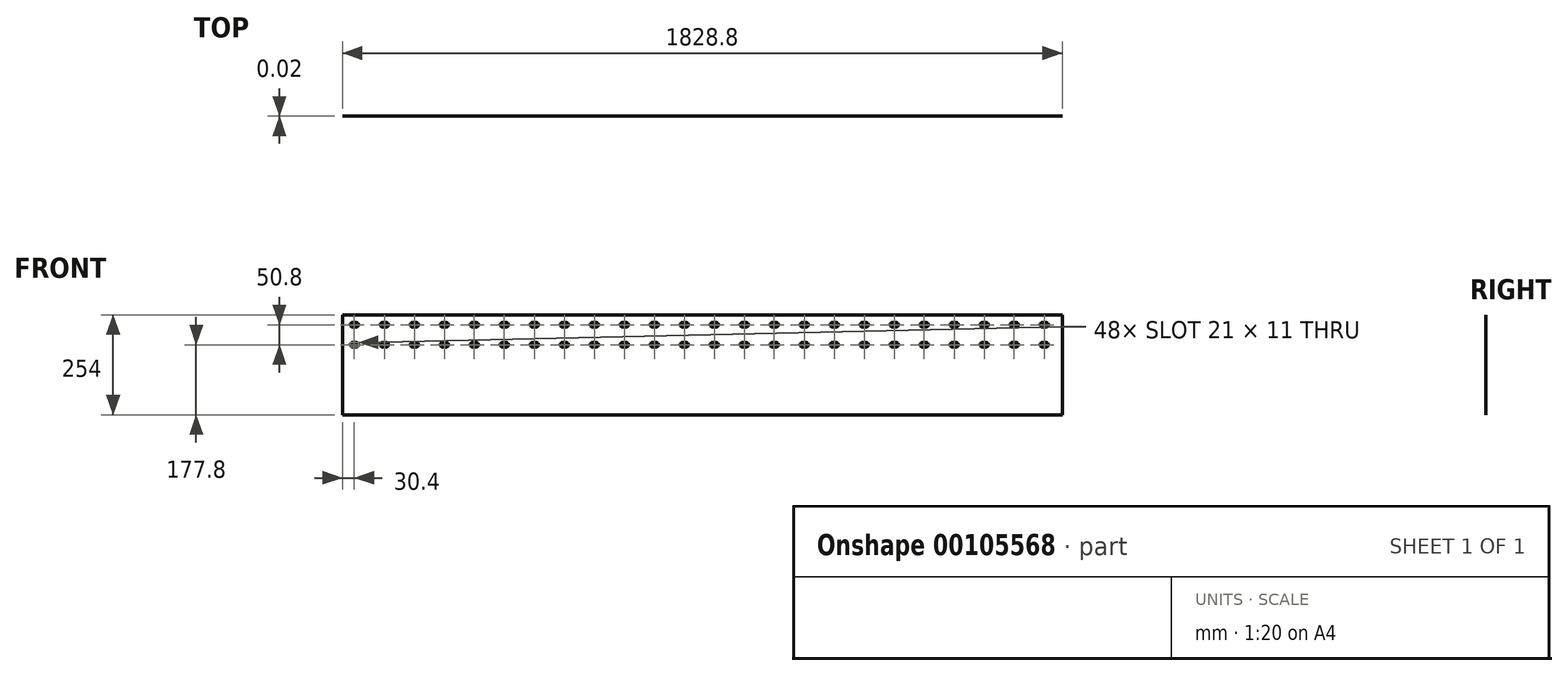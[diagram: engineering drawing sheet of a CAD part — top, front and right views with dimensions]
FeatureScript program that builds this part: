
annotation { "Feature Type Name" : "Feature", "Feature Type Description" : "" }
export const myFeature = defineFeature(function(context is Context, id is Id, definition is map)
    precondition{}
    {
        {
            var Q0;
            Q0=qCreatedBy(makeId("Front.planeOp"),FACE);
            var sketch = newSketch(context, id + "F0", { "sketchPlane" : qUnion([Q0])});
            skLineSegment(sketch, "E0.bottom", {"start": v(1828.8, 254) * mm, "end": v(0, 254) * mm});
            skLineSegment(sketch, "E0.top", {"start": v(1828.8, 0) * mm, "end": v(0, 0) * mm});
            skLineSegment(sketch, "E0.left", {"start": v(1828.8, 254) * mm, "end": v(1828.8, 0) * mm});
            skLineSegment(sketch, "E0.right", {"start": v(0, 254) * mm, "end": v(0, 0) * mm});
            skLineSegment(sketch, "E1", {"start": v(0, 152.4) * mm, "end": v(1828.8, 152.4) * mm, "construction": true});
            skSolve(sketch);
        }
        {
            var Q0;
            Q0=makeQuery(id+"F0.imprint","IMPRINT",FACE,{"disambiguationData":[TD([[makeQuery(id+"F0.imprint","IMPRINT",EDGE,{"derivedFrom":sQuery(id+"F0.wireOp",EDGE,"E0.bottom")}),1.0]])]});
            extrude(context, id + "F1", {"entities" : qUnion([Q0]), "depth" : 0.31 / 50.8 * mm, "hasSecondDirection" : true, "secondDirectionOppositeDirection" : true, "secondDirectionDepth" : 0.31 / 50.8 * mm});
        }
        {
            var Q0;
            Q0=makeQuery(id+"F1.opExtrude","CAP_FACE",FACE,{"disambiguationData":[OSD([sQuery(id+"F0.wireOp",EDGE,"E0.bottom"),sQuery(id+"F0.wireOp",EDGE,"E0.top"),sQuery(id+"F0.wireOp",EDGE,"E0.left"),sQuery(id+"F0.wireOp",EDGE,"E0.right")])],"isStart":false});
            var sketch = newSketch(context, id + "F2", { "sketchPlane" : qUnion([Q0])});
            skArc(sketch, "E2", {"start": v(25.4, 234.1) * mm, "mid": v(19.9, 228.6) * mm, "end": v(25.4, 223.1) * mm});
            skArc(sketch, "E3", {"start": v(35.4, 223.1) * mm, "mid": v(40.9, 228.6) * mm, "end": v(35.4, 234.1) * mm});
            skLineSegment(sketch, "E4", {"start": v(25.4, 234.1) * mm, "end": v(35.4, 234.1) * mm});
            skLineSegment(sketch, "E5", {"start": v(35.4, 223.1) * mm, "end": v(25.4, 223.1) * mm});
            skLineSegment(sketch, "E6.0.1.0", {"start": v(35.4, 172.3) * mm, "end": v(25.4, 172.3) * mm});
            skArc(sketch, "E6.0.1.1", {"start": v(25.4, 183.3) * mm, "mid": v(19.9, 177.8) * mm, "end": v(25.4, 172.3) * mm});
            skLineSegment(sketch, "E6.0.1.2", {"start": v(25.4, 183.3) * mm, "end": v(35.4, 183.3) * mm});
            skArc(sketch, "E6.0.1.3", {"start": v(35.4, 172.3) * mm, "mid": v(40.9, 177.8) * mm, "end": v(35.4, 183.3) * mm});
            skLineSegment(sketch, "E6.1.0.0", {"start": v(111.6, 223.1) * mm, "end": v(101.6, 223.1) * mm});
            skArc(sketch, "E6.1.0.1", {"start": v(101.6, 234.1) * mm, "mid": v(96.1, 228.6) * mm, "end": v(101.6, 223.1) * mm});
            skLineSegment(sketch, "E6.1.0.2", {"start": v(101.6, 234.1) * mm, "end": v(111.6, 234.1) * mm});
            skArc(sketch, "E6.1.0.3", {"start": v(111.6, 223.1) * mm, "mid": v(117.1, 228.6) * mm, "end": v(111.6, 234.1) * mm});
            skLineSegment(sketch, "E6.1.1.0", {"start": v(111.6, 172.3) * mm, "end": v(101.6, 172.3) * mm});
            skArc(sketch, "E6.1.1.1", {"start": v(101.6, 183.3) * mm, "mid": v(96.1, 177.8) * mm, "end": v(101.6, 172.3) * mm});
            skLineSegment(sketch, "E6.1.1.2", {"start": v(101.6, 183.3) * mm, "end": v(111.6, 183.3) * mm});
            skArc(sketch, "E6.1.1.3", {"start": v(111.6, 172.3) * mm, "mid": v(117.1, 177.8) * mm, "end": v(111.6, 183.3) * mm});
            skLineSegment(sketch, "E6.2.0.0", {"start": v(187.8, 223.1) * mm, "end": v(177.8, 223.1) * mm});
            skArc(sketch, "E6.2.0.1", {"start": v(177.8, 234.1) * mm, "mid": v(172.3, 228.6) * mm, "end": v(177.8, 223.1) * mm});
            skLineSegment(sketch, "E6.2.0.2", {"start": v(177.8, 234.1) * mm, "end": v(187.8, 234.1) * mm});
            skArc(sketch, "E6.2.0.3", {"start": v(187.8, 223.1) * mm, "mid": v(193.3, 228.6) * mm, "end": v(187.8, 234.1) * mm});
            skLineSegment(sketch, "E6.2.1.0", {"start": v(187.8, 172.3) * mm, "end": v(177.8, 172.3) * mm});
            skArc(sketch, "E6.2.1.1", {"start": v(177.8, 183.3) * mm, "mid": v(172.3, 177.8) * mm, "end": v(177.8, 172.3) * mm});
            skLineSegment(sketch, "E6.2.1.2", {"start": v(177.8, 183.3) * mm, "end": v(187.8, 183.3) * mm});
            skArc(sketch, "E6.2.1.3", {"start": v(187.8, 172.3) * mm, "mid": v(193.3, 177.8) * mm, "end": v(187.8, 183.3) * mm});
            skLineSegment(sketch, "E6.3.0.0", {"start": v(264, 223.1) * mm, "end": v(254, 223.1) * mm});
            skArc(sketch, "E6.3.0.1", {"start": v(254, 234.1) * mm, "mid": v(248.5, 228.6) * mm, "end": v(254, 223.1) * mm});
            skLineSegment(sketch, "E6.3.0.2", {"start": v(254, 234.1) * mm, "end": v(264, 234.1) * mm});
            skArc(sketch, "E6.3.0.3", {"start": v(264, 223.1) * mm, "mid": v(269.5, 228.6) * mm, "end": v(264, 234.1) * mm});
            skLineSegment(sketch, "E6.3.1.0", {"start": v(264, 172.3) * mm, "end": v(254, 172.3) * mm});
            skArc(sketch, "E6.3.1.1", {"start": v(254, 183.3) * mm, "mid": v(248.5, 177.8) * mm, "end": v(254, 172.3) * mm});
            skLineSegment(sketch, "E6.3.1.2", {"start": v(254, 183.3) * mm, "end": v(264, 183.3) * mm});
            skArc(sketch, "E6.3.1.3", {"start": v(264, 172.3) * mm, "mid": v(269.5, 177.8) * mm, "end": v(264, 183.3) * mm});
            skLineSegment(sketch, "E6.4.0.0", {"start": v(340.2, 223.1) * mm, "end": v(330.2, 223.1) * mm});
            skArc(sketch, "E6.4.0.1", {"start": v(330.2, 234.1) * mm, "mid": v(324.7, 228.6) * mm, "end": v(330.2, 223.1) * mm});
            skLineSegment(sketch, "E6.4.0.2", {"start": v(330.2, 234.1) * mm, "end": v(340.2, 234.1) * mm});
            skArc(sketch, "E6.4.0.3", {"start": v(340.2, 223.1) * mm, "mid": v(345.7, 228.6) * mm, "end": v(340.2, 234.1) * mm});
            skLineSegment(sketch, "E6.4.1.0", {"start": v(340.2, 172.3) * mm, "end": v(330.2, 172.3) * mm});
            skArc(sketch, "E6.4.1.1", {"start": v(330.2, 183.3) * mm, "mid": v(324.7, 177.8) * mm, "end": v(330.2, 172.3) * mm});
            skLineSegment(sketch, "E6.4.1.2", {"start": v(330.2, 183.3) * mm, "end": v(340.2, 183.3) * mm});
            skArc(sketch, "E6.4.1.3", {"start": v(340.2, 172.3) * mm, "mid": v(345.7, 177.8) * mm, "end": v(340.2, 183.3) * mm});
            skLineSegment(sketch, "E6.5.0.0", {"start": v(416.4, 223.1) * mm, "end": v(406.4, 223.1) * mm});
            skArc(sketch, "E6.5.0.1", {"start": v(406.4, 234.1) * mm, "mid": v(400.9, 228.6) * mm, "end": v(406.4, 223.1) * mm});
            skLineSegment(sketch, "E6.5.0.2", {"start": v(406.4, 234.1) * mm, "end": v(416.4, 234.1) * mm});
            skArc(sketch, "E6.5.0.3", {"start": v(416.4, 223.1) * mm, "mid": v(421.9, 228.6) * mm, "end": v(416.4, 234.1) * mm});
            skLineSegment(sketch, "E6.5.1.0", {"start": v(416.4, 172.3) * mm, "end": v(406.4, 172.3) * mm});
            skArc(sketch, "E6.5.1.1", {"start": v(406.4, 183.3) * mm, "mid": v(400.9, 177.8) * mm, "end": v(406.4, 172.3) * mm});
            skLineSegment(sketch, "E6.5.1.2", {"start": v(406.4, 183.3) * mm, "end": v(416.4, 183.3) * mm});
            skArc(sketch, "E6.5.1.3", {"start": v(416.4, 172.3) * mm, "mid": v(421.9, 177.8) * mm, "end": v(416.4, 183.3) * mm});
            skLineSegment(sketch, "E6.6.0.0", {"start": v(492.6, 223.1) * mm, "end": v(482.6, 223.1) * mm});
            skArc(sketch, "E6.6.0.1", {"start": v(482.6, 234.1) * mm, "mid": v(477.1, 228.6) * mm, "end": v(482.6, 223.1) * mm});
            skLineSegment(sketch, "E6.6.0.2", {"start": v(482.6, 234.1) * mm, "end": v(492.6, 234.1) * mm});
            skArc(sketch, "E6.6.0.3", {"start": v(492.6, 223.1) * mm, "mid": v(498.1, 228.6) * mm, "end": v(492.6, 234.1) * mm});
            skLineSegment(sketch, "E6.6.1.0", {"start": v(492.6, 172.3) * mm, "end": v(482.6, 172.3) * mm});
            skArc(sketch, "E6.6.1.1", {"start": v(482.6, 183.3) * mm, "mid": v(477.1, 177.8) * mm, "end": v(482.6, 172.3) * mm});
            skLineSegment(sketch, "E6.6.1.2", {"start": v(482.6, 183.3) * mm, "end": v(492.6, 183.3) * mm});
            skArc(sketch, "E6.6.1.3", {"start": v(492.6, 172.3) * mm, "mid": v(498.1, 177.8) * mm, "end": v(492.6, 183.3) * mm});
            skLineSegment(sketch, "E6.7.0.0", {"start": v(568.8, 223.1) * mm, "end": v(558.8, 223.1) * mm});
            skArc(sketch, "E6.7.0.1", {"start": v(558.8, 234.1) * mm, "mid": v(553.3, 228.6) * mm, "end": v(558.8, 223.1) * mm});
            skLineSegment(sketch, "E6.7.0.2", {"start": v(558.8, 234.1) * mm, "end": v(568.8, 234.1) * mm});
            skArc(sketch, "E6.7.0.3", {"start": v(568.8, 223.1) * mm, "mid": v(574.3, 228.6) * mm, "end": v(568.8, 234.1) * mm});
            skLineSegment(sketch, "E6.7.1.0", {"start": v(568.8, 172.3) * mm, "end": v(558.8, 172.3) * mm});
            skArc(sketch, "E6.7.1.1", {"start": v(558.8, 183.3) * mm, "mid": v(553.3, 177.8) * mm, "end": v(558.8, 172.3) * mm});
            skLineSegment(sketch, "E6.7.1.2", {"start": v(558.8, 183.3) * mm, "end": v(568.8, 183.3) * mm});
            skArc(sketch, "E6.7.1.3", {"start": v(568.8, 172.3) * mm, "mid": v(574.3, 177.8) * mm, "end": v(568.8, 183.3) * mm});
            skLineSegment(sketch, "E6.8.0.0", {"start": v(645, 223.1) * mm, "end": v(635, 223.1) * mm});
            skArc(sketch, "E6.8.0.1", {"start": v(635, 234.1) * mm, "mid": v(629.5, 228.6) * mm, "end": v(635, 223.1) * mm});
            skLineSegment(sketch, "E6.8.0.2", {"start": v(635, 234.1) * mm, "end": v(645, 234.1) * mm});
            skArc(sketch, "E6.8.0.3", {"start": v(645, 223.1) * mm, "mid": v(650.5, 228.6) * mm, "end": v(645, 234.1) * mm});
            skLineSegment(sketch, "E6.8.1.0", {"start": v(645, 172.3) * mm, "end": v(635, 172.3) * mm});
            skArc(sketch, "E6.8.1.1", {"start": v(635, 183.3) * mm, "mid": v(629.5, 177.8) * mm, "end": v(635, 172.3) * mm});
            skLineSegment(sketch, "E6.8.1.2", {"start": v(635, 183.3) * mm, "end": v(645, 183.3) * mm});
            skArc(sketch, "E6.8.1.3", {"start": v(645, 172.3) * mm, "mid": v(650.5, 177.8) * mm, "end": v(645, 183.3) * mm});
            skLineSegment(sketch, "E6.9.0.0", {"start": v(721.2, 223.1) * mm, "end": v(711.2, 223.1) * mm});
            skArc(sketch, "E6.9.0.1", {"start": v(711.2, 234.1) * mm, "mid": v(705.7, 228.6) * mm, "end": v(711.2, 223.1) * mm});
            skLineSegment(sketch, "E6.9.0.2", {"start": v(711.2, 234.1) * mm, "end": v(721.2, 234.1) * mm});
            skArc(sketch, "E6.9.0.3", {"start": v(721.2, 223.1) * mm, "mid": v(726.7, 228.6) * mm, "end": v(721.2, 234.1) * mm});
            skLineSegment(sketch, "E6.9.1.0", {"start": v(721.2, 172.3) * mm, "end": v(711.2, 172.3) * mm});
            skArc(sketch, "E6.9.1.1", {"start": v(711.2, 183.3) * mm, "mid": v(705.7, 177.8) * mm, "end": v(711.2, 172.3) * mm});
            skLineSegment(sketch, "E6.9.1.2", {"start": v(711.2, 183.3) * mm, "end": v(721.2, 183.3) * mm});
            skArc(sketch, "E6.9.1.3", {"start": v(721.2, 172.3) * mm, "mid": v(726.7, 177.8) * mm, "end": v(721.2, 183.3) * mm});
            skLineSegment(sketch, "E6.10.0.0", {"start": v(797.4, 223.1) * mm, "end": v(787.4, 223.1) * mm});
            skArc(sketch, "E6.10.0.1", {"start": v(787.4, 234.1) * mm, "mid": v(781.9, 228.6) * mm, "end": v(787.4, 223.1) * mm});
            skLineSegment(sketch, "E6.10.0.2", {"start": v(787.4, 234.1) * mm, "end": v(797.4, 234.1) * mm});
            skArc(sketch, "E6.10.0.3", {"start": v(797.4, 223.1) * mm, "mid": v(802.9, 228.6) * mm, "end": v(797.4, 234.1) * mm});
            skLineSegment(sketch, "E6.10.1.0", {"start": v(797.4, 172.3) * mm, "end": v(787.4, 172.3) * mm});
            skArc(sketch, "E6.10.1.1", {"start": v(787.4, 183.3) * mm, "mid": v(781.9, 177.8) * mm, "end": v(787.4, 172.3) * mm});
            skLineSegment(sketch, "E6.10.1.2", {"start": v(787.4, 183.3) * mm, "end": v(797.4, 183.3) * mm});
            skArc(sketch, "E6.10.1.3", {"start": v(797.4, 172.3) * mm, "mid": v(802.9, 177.8) * mm, "end": v(797.4, 183.3) * mm});
            skLineSegment(sketch, "E6.11.0.0", {"start": v(873.6, 223.1) * mm, "end": v(863.6, 223.1) * mm});
            skArc(sketch, "E6.11.0.1", {"start": v(863.6, 234.1) * mm, "mid": v(858.1, 228.6) * mm, "end": v(863.6, 223.1) * mm});
            skLineSegment(sketch, "E6.11.0.2", {"start": v(863.6, 234.1) * mm, "end": v(873.6, 234.1) * mm});
            skArc(sketch, "E6.11.0.3", {"start": v(873.6, 223.1) * mm, "mid": v(879.1, 228.6) * mm, "end": v(873.6, 234.1) * mm});
            skLineSegment(sketch, "E6.11.1.0", {"start": v(873.6, 172.3) * mm, "end": v(863.6, 172.3) * mm});
            skArc(sketch, "E6.11.1.1", {"start": v(863.6, 183.3) * mm, "mid": v(858.1, 177.8) * mm, "end": v(863.6, 172.3) * mm});
            skLineSegment(sketch, "E6.11.1.2", {"start": v(863.6, 183.3) * mm, "end": v(873.6, 183.3) * mm});
            skArc(sketch, "E6.11.1.3", {"start": v(873.6, 172.3) * mm, "mid": v(879.1, 177.8) * mm, "end": v(873.6, 183.3) * mm});
            skLineSegment(sketch, "E6.12.0.0", {"start": v(949.8, 223.1) * mm, "end": v(939.8, 223.1) * mm});
            skArc(sketch, "E6.12.0.1", {"start": v(939.8, 234.1) * mm, "mid": v(934.3, 228.6) * mm, "end": v(939.8, 223.1) * mm});
            skLineSegment(sketch, "E6.12.0.2", {"start": v(939.8, 234.1) * mm, "end": v(949.8, 234.1) * mm});
            skArc(sketch, "E6.12.0.3", {"start": v(949.8, 223.1) * mm, "mid": v(955.3, 228.6) * mm, "end": v(949.8, 234.1) * mm});
            skLineSegment(sketch, "E6.12.1.0", {"start": v(949.8, 172.3) * mm, "end": v(939.8, 172.3) * mm});
            skArc(sketch, "E6.12.1.1", {"start": v(939.8, 183.3) * mm, "mid": v(934.3, 177.8) * mm, "end": v(939.8, 172.3) * mm});
            skLineSegment(sketch, "E6.12.1.2", {"start": v(939.8, 183.3) * mm, "end": v(949.8, 183.3) * mm});
            skArc(sketch, "E6.12.1.3", {"start": v(949.8, 172.3) * mm, "mid": v(955.3, 177.8) * mm, "end": v(949.8, 183.3) * mm});
            skLineSegment(sketch, "E6.13.0.0", {"start": v(1026, 223.1) * mm, "end": v(1016, 223.1) * mm});
            skArc(sketch, "E6.13.0.1", {"start": v(1016, 234.1) * mm, "mid": v(1010.5, 228.6) * mm, "end": v(1016, 223.1) * mm});
            skLineSegment(sketch, "E6.13.0.2", {"start": v(1016, 234.1) * mm, "end": v(1026, 234.1) * mm});
            skArc(sketch, "E6.13.0.3", {"start": v(1026, 223.1) * mm, "mid": v(1031.5, 228.6) * mm, "end": v(1026, 234.1) * mm});
            skLineSegment(sketch, "E6.13.1.0", {"start": v(1026, 172.3) * mm, "end": v(1016, 172.3) * mm});
            skArc(sketch, "E6.13.1.1", {"start": v(1016, 183.3) * mm, "mid": v(1010.5, 177.8) * mm, "end": v(1016, 172.3) * mm});
            skLineSegment(sketch, "E6.13.1.2", {"start": v(1016, 183.3) * mm, "end": v(1026, 183.3) * mm});
            skArc(sketch, "E6.13.1.3", {"start": v(1026, 172.3) * mm, "mid": v(1031.5, 177.8) * mm, "end": v(1026, 183.3) * mm});
            skLineSegment(sketch, "E6.14.0.0", {"start": v(1102.2, 223.1) * mm, "end": v(1092.2, 223.1) * mm});
            skArc(sketch, "E6.14.0.1", {"start": v(1092.2, 234.1) * mm, "mid": v(1086.7, 228.6) * mm, "end": v(1092.2, 223.1) * mm});
            skLineSegment(sketch, "E6.14.0.2", {"start": v(1092.2, 234.1) * mm, "end": v(1102.2, 234.1) * mm});
            skArc(sketch, "E6.14.0.3", {"start": v(1102.2, 223.1) * mm, "mid": v(1107.7, 228.6) * mm, "end": v(1102.2, 234.1) * mm});
            skLineSegment(sketch, "E6.14.1.0", {"start": v(1102.2, 172.3) * mm, "end": v(1092.2, 172.3) * mm});
            skArc(sketch, "E6.14.1.1", {"start": v(1092.2, 183.3) * mm, "mid": v(1086.7, 177.8) * mm, "end": v(1092.2, 172.3) * mm});
            skLineSegment(sketch, "E6.14.1.2", {"start": v(1092.2, 183.3) * mm, "end": v(1102.2, 183.3) * mm});
            skArc(sketch, "E6.14.1.3", {"start": v(1102.2, 172.3) * mm, "mid": v(1107.7, 177.8) * mm, "end": v(1102.2, 183.3) * mm});
            skLineSegment(sketch, "E6.15.0.0", {"start": v(1178.4, 223.1) * mm, "end": v(1168.4, 223.1) * mm});
            skArc(sketch, "E6.15.0.1", {"start": v(1168.4, 234.1) * mm, "mid": v(1162.9, 228.6) * mm, "end": v(1168.4, 223.1) * mm});
            skLineSegment(sketch, "E6.15.0.2", {"start": v(1168.4, 234.1) * mm, "end": v(1178.4, 234.1) * mm});
            skArc(sketch, "E6.15.0.3", {"start": v(1178.4, 223.1) * mm, "mid": v(1183.9, 228.6) * mm, "end": v(1178.4, 234.1) * mm});
            skLineSegment(sketch, "E6.15.1.0", {"start": v(1178.4, 172.3) * mm, "end": v(1168.4, 172.3) * mm});
            skArc(sketch, "E6.15.1.1", {"start": v(1168.4, 183.3) * mm, "mid": v(1162.9, 177.8) * mm, "end": v(1168.4, 172.3) * mm});
            skLineSegment(sketch, "E6.15.1.2", {"start": v(1168.4, 183.3) * mm, "end": v(1178.4, 183.3) * mm});
            skArc(sketch, "E6.15.1.3", {"start": v(1178.4, 172.3) * mm, "mid": v(1183.9, 177.8) * mm, "end": v(1178.4, 183.3) * mm});
            skLineSegment(sketch, "E6.16.0.0", {"start": v(1254.6, 223.1) * mm, "end": v(1244.6, 223.1) * mm});
            skArc(sketch, "E6.16.0.1", {"start": v(1244.6, 234.1) * mm, "mid": v(1239.1, 228.6) * mm, "end": v(1244.6, 223.1) * mm});
            skLineSegment(sketch, "E6.16.0.2", {"start": v(1244.6, 234.1) * mm, "end": v(1254.6, 234.1) * mm});
            skArc(sketch, "E6.16.0.3", {"start": v(1254.6, 223.1) * mm, "mid": v(1260.1, 228.6) * mm, "end": v(1254.6, 234.1) * mm});
            skLineSegment(sketch, "E6.16.1.0", {"start": v(1254.6, 172.3) * mm, "end": v(1244.6, 172.3) * mm});
            skArc(sketch, "E6.16.1.1", {"start": v(1244.6, 183.3) * mm, "mid": v(1239.1, 177.8) * mm, "end": v(1244.6, 172.3) * mm});
            skLineSegment(sketch, "E6.16.1.2", {"start": v(1244.6, 183.3) * mm, "end": v(1254.6, 183.3) * mm});
            skArc(sketch, "E6.16.1.3", {"start": v(1254.6, 172.3) * mm, "mid": v(1260.1, 177.8) * mm, "end": v(1254.6, 183.3) * mm});
            skLineSegment(sketch, "E6.17.0.0", {"start": v(1330.8, 223.1) * mm, "end": v(1320.8, 223.1) * mm});
            skArc(sketch, "E6.17.0.1", {"start": v(1320.8, 234.1) * mm, "mid": v(1315.3, 228.6) * mm, "end": v(1320.8, 223.1) * mm});
            skLineSegment(sketch, "E6.17.0.2", {"start": v(1320.8, 234.1) * mm, "end": v(1330.8, 234.1) * mm});
            skArc(sketch, "E6.17.0.3", {"start": v(1330.8, 223.1) * mm, "mid": v(1336.3, 228.6) * mm, "end": v(1330.8, 234.1) * mm});
            skLineSegment(sketch, "E6.17.1.0", {"start": v(1330.8, 172.3) * mm, "end": v(1320.8, 172.3) * mm});
            skArc(sketch, "E6.17.1.1", {"start": v(1320.8, 183.3) * mm, "mid": v(1315.3, 177.8) * mm, "end": v(1320.8, 172.3) * mm});
            skLineSegment(sketch, "E6.17.1.2", {"start": v(1320.8, 183.3) * mm, "end": v(1330.8, 183.3) * mm});
            skArc(sketch, "E6.17.1.3", {"start": v(1330.8, 172.3) * mm, "mid": v(1336.3, 177.8) * mm, "end": v(1330.8, 183.3) * mm});
            skLineSegment(sketch, "E6.18.0.0", {"start": v(1407, 223.1) * mm, "end": v(1397, 223.1) * mm});
            skArc(sketch, "E6.18.0.1", {"start": v(1397, 234.1) * mm, "mid": v(1391.5, 228.6) * mm, "end": v(1397, 223.1) * mm});
            skLineSegment(sketch, "E6.18.0.2", {"start": v(1397, 234.1) * mm, "end": v(1407, 234.1) * mm});
            skArc(sketch, "E6.18.0.3", {"start": v(1407, 223.1) * mm, "mid": v(1412.5, 228.6) * mm, "end": v(1407, 234.1) * mm});
            skLineSegment(sketch, "E6.18.1.0", {"start": v(1407, 172.3) * mm, "end": v(1397, 172.3) * mm});
            skArc(sketch, "E6.18.1.1", {"start": v(1397, 183.3) * mm, "mid": v(1391.5, 177.8) * mm, "end": v(1397, 172.3) * mm});
            skLineSegment(sketch, "E6.18.1.2", {"start": v(1397, 183.3) * mm, "end": v(1407, 183.3) * mm});
            skArc(sketch, "E6.18.1.3", {"start": v(1407, 172.3) * mm, "mid": v(1412.5, 177.8) * mm, "end": v(1407, 183.3) * mm});
            skLineSegment(sketch, "E6.19.0.0", {"start": v(1483.2, 223.1) * mm, "end": v(1473.2, 223.1) * mm});
            skArc(sketch, "E6.19.0.1", {"start": v(1473.2, 234.1) * mm, "mid": v(1467.7, 228.6) * mm, "end": v(1473.2, 223.1) * mm});
            skLineSegment(sketch, "E6.19.0.2", {"start": v(1473.2, 234.1) * mm, "end": v(1483.2, 234.1) * mm});
            skArc(sketch, "E6.19.0.3", {"start": v(1483.2, 223.1) * mm, "mid": v(1488.7, 228.6) * mm, "end": v(1483.2, 234.1) * mm});
            skLineSegment(sketch, "E6.19.1.0", {"start": v(1483.2, 172.3) * mm, "end": v(1473.2, 172.3) * mm});
            skArc(sketch, "E6.19.1.1", {"start": v(1473.2, 183.3) * mm, "mid": v(1467.7, 177.8) * mm, "end": v(1473.2, 172.3) * mm});
            skLineSegment(sketch, "E6.19.1.2", {"start": v(1473.2, 183.3) * mm, "end": v(1483.2, 183.3) * mm});
            skArc(sketch, "E6.19.1.3", {"start": v(1483.2, 172.3) * mm, "mid": v(1488.7, 177.8) * mm, "end": v(1483.2, 183.3) * mm});
            skLineSegment(sketch, "E6.20.0.0", {"start": v(1559.4, 223.1) * mm, "end": v(1549.4, 223.1) * mm});
            skArc(sketch, "E6.20.0.1", {"start": v(1549.4, 234.1) * mm, "mid": v(1543.9, 228.6) * mm, "end": v(1549.4, 223.1) * mm});
            skLineSegment(sketch, "E6.20.0.2", {"start": v(1549.4, 234.1) * mm, "end": v(1559.4, 234.1) * mm});
            skArc(sketch, "E6.20.0.3", {"start": v(1559.4, 223.1) * mm, "mid": v(1564.9, 228.6) * mm, "end": v(1559.4, 234.1) * mm});
            skLineSegment(sketch, "E6.20.1.0", {"start": v(1559.4, 172.3) * mm, "end": v(1549.4, 172.3) * mm});
            skArc(sketch, "E6.20.1.1", {"start": v(1549.4, 183.3) * mm, "mid": v(1543.9, 177.8) * mm, "end": v(1549.4, 172.3) * mm});
            skLineSegment(sketch, "E6.20.1.2", {"start": v(1549.4, 183.3) * mm, "end": v(1559.4, 183.3) * mm});
            skArc(sketch, "E6.20.1.3", {"start": v(1559.4, 172.3) * mm, "mid": v(1564.9, 177.8) * mm, "end": v(1559.4, 183.3) * mm});
            skLineSegment(sketch, "E6.21.0.0", {"start": v(1635.6, 223.1) * mm, "end": v(1625.6, 223.1) * mm});
            skArc(sketch, "E6.21.0.1", {"start": v(1625.6, 234.1) * mm, "mid": v(1620.1, 228.6) * mm, "end": v(1625.6, 223.1) * mm});
            skLineSegment(sketch, "E6.21.0.2", {"start": v(1625.6, 234.1) * mm, "end": v(1635.6, 234.1) * mm});
            skArc(sketch, "E6.21.0.3", {"start": v(1635.6, 223.1) * mm, "mid": v(1641.1, 228.6) * mm, "end": v(1635.6, 234.1) * mm});
            skLineSegment(sketch, "E6.21.1.0", {"start": v(1635.6, 172.3) * mm, "end": v(1625.6, 172.3) * mm});
            skArc(sketch, "E6.21.1.1", {"start": v(1625.6, 183.3) * mm, "mid": v(1620.1, 177.8) * mm, "end": v(1625.6, 172.3) * mm});
            skLineSegment(sketch, "E6.21.1.2", {"start": v(1625.6, 183.3) * mm, "end": v(1635.6, 183.3) * mm});
            skArc(sketch, "E6.21.1.3", {"start": v(1635.6, 172.3) * mm, "mid": v(1641.1, 177.8) * mm, "end": v(1635.6, 183.3) * mm});
            skLineSegment(sketch, "E6.22.0.0", {"start": v(1711.8, 223.1) * mm, "end": v(1701.8, 223.1) * mm});
            skArc(sketch, "E6.22.0.1", {"start": v(1701.8, 234.1) * mm, "mid": v(1696.3, 228.6) * mm, "end": v(1701.8, 223.1) * mm});
            skLineSegment(sketch, "E6.22.0.2", {"start": v(1701.8, 234.1) * mm, "end": v(1711.8, 234.1) * mm});
            skArc(sketch, "E6.22.0.3", {"start": v(1711.8, 223.1) * mm, "mid": v(1717.3, 228.6) * mm, "end": v(1711.8, 234.1) * mm});
            skLineSegment(sketch, "E6.22.1.0", {"start": v(1711.8, 172.3) * mm, "end": v(1701.8, 172.3) * mm});
            skArc(sketch, "E6.22.1.1", {"start": v(1701.8, 183.3) * mm, "mid": v(1696.3, 177.8) * mm, "end": v(1701.8, 172.3) * mm});
            skLineSegment(sketch, "E6.22.1.2", {"start": v(1701.8, 183.3) * mm, "end": v(1711.8, 183.3) * mm});
            skArc(sketch, "E6.22.1.3", {"start": v(1711.8, 172.3) * mm, "mid": v(1717.3, 177.8) * mm, "end": v(1711.8, 183.3) * mm});
            skLineSegment(sketch, "E6.23.0.0", {"start": v(1788, 223.1) * mm, "end": v(1778, 223.1) * mm});
            skArc(sketch, "E6.23.0.1", {"start": v(1778, 234.1) * mm, "mid": v(1772.5, 228.6) * mm, "end": v(1778, 223.1) * mm});
            skLineSegment(sketch, "E6.23.0.2", {"start": v(1778, 234.1) * mm, "end": v(1788, 234.1) * mm});
            skArc(sketch, "E6.23.0.3", {"start": v(1788, 223.1) * mm, "mid": v(1793.5, 228.6) * mm, "end": v(1788, 234.1) * mm});
            skLineSegment(sketch, "E6.23.1.0", {"start": v(1788, 172.3) * mm, "end": v(1778, 172.3) * mm});
            skArc(sketch, "E6.23.1.1", {"start": v(1778, 183.3) * mm, "mid": v(1772.5, 177.8) * mm, "end": v(1778, 172.3) * mm});
            skLineSegment(sketch, "E6.23.1.2", {"start": v(1778, 183.3) * mm, "end": v(1788, 183.3) * mm});
            skArc(sketch, "E6.23.1.3", {"start": v(1788, 172.3) * mm, "mid": v(1793.5, 177.8) * mm, "end": v(1788, 183.3) * mm});
            skLineSegment(sketch, "E6.direction1", {"start": v(25.4, 223.1) * mm, "end": v(101.6, 223.1) * mm, "construction": true});
            skLineSegment(sketch, "E6.direction2", {"start": v(25.4, 223.1) * mm, "end": v(25.4, 172.3) * mm, "construction": true});
            skSolve(sketch);
        }
        {
            var Q0;
            Q0=makeQuery(id+"F2.imprint","IMPRINT",FACE,{"disambiguationData":[TD([[makeQuery(id+"F2.imprint","IMPRINT",EDGE,{"derivedFrom":sQuery(id+"F2.wireOp",EDGE,"E2")}),1.0]])]});
            var Q1;
            Q1=makeQuery(id+"F2.imprint","IMPRINT",FACE,{"disambiguationData":[TD([[makeQuery(id+"F2.imprint","IMPRINT",EDGE,{"derivedFrom":sQuery(id+"F2.wireOp",EDGE,"E6.1.0.0")}),-1.0]])]});
            var Q2;
            Q2=makeQuery(id+"F2.imprint","IMPRINT",FACE,{"disambiguationData":[TD([[makeQuery(id+"F2.imprint","IMPRINT",EDGE,{"derivedFrom":sQuery(id+"F2.wireOp",EDGE,"E6.1.1.0")}),-1.0]])]});
            var Q3;
            Q3=makeQuery(id+"F2.imprint","IMPRINT",FACE,{"disambiguationData":[TD([[makeQuery(id+"F2.imprint","IMPRINT",EDGE,{"derivedFrom":sQuery(id+"F2.wireOp",EDGE,"E6.0.1.0")}),-1.0]])]});
            var Q4;
            Q4=makeQuery(id+"F2.imprint","IMPRINT",FACE,{"disambiguationData":[TD([[makeQuery(id+"F2.imprint","IMPRINT",EDGE,{"derivedFrom":sQuery(id+"F2.wireOp",EDGE,"E6.2.0.0")}),-1.0]])]});
            var Q5;
            Q5=makeQuery(id+"F2.imprint","IMPRINT",FACE,{"disambiguationData":[TD([[makeQuery(id+"F2.imprint","IMPRINT",EDGE,{"derivedFrom":sQuery(id+"F2.wireOp",EDGE,"E6.2.1.0")}),-1.0]])]});
            var Q6;
            Q6=makeQuery(id+"F2.imprint","IMPRINT",FACE,{"disambiguationData":[TD([[makeQuery(id+"F2.imprint","IMPRINT",EDGE,{"derivedFrom":sQuery(id+"F2.wireOp",EDGE,"E6.3.0.0")}),-1.0]])]});
            var Q7;
            Q7=makeQuery(id+"F2.imprint","IMPRINT",FACE,{"disambiguationData":[TD([[makeQuery(id+"F2.imprint","IMPRINT",EDGE,{"derivedFrom":sQuery(id+"F2.wireOp",EDGE,"E6.3.1.0")}),-1.0]])]});
            var Q8;
            Q8=makeQuery(id+"F2.imprint","IMPRINT",FACE,{"disambiguationData":[TD([[makeQuery(id+"F2.imprint","IMPRINT",EDGE,{"derivedFrom":sQuery(id+"F2.wireOp",EDGE,"E6.4.1.0")}),-1.0]])]});
            var Q9;
            Q9=makeQuery(id+"F2.imprint","IMPRINT",FACE,{"disambiguationData":[TD([[makeQuery(id+"F2.imprint","IMPRINT",EDGE,{"derivedFrom":sQuery(id+"F2.wireOp",EDGE,"E6.4.0.0")}),-1.0]])]});
            var Q10;
            Q10=makeQuery(id+"F2.imprint","IMPRINT",FACE,{"disambiguationData":[TD([[makeQuery(id+"F2.imprint","IMPRINT",EDGE,{"derivedFrom":sQuery(id+"F2.wireOp",EDGE,"E6.5.0.0")}),-1.0]])]});
            var Q11;
            Q11=makeQuery(id+"F2.imprint","IMPRINT",FACE,{"disambiguationData":[TD([[makeQuery(id+"F2.imprint","IMPRINT",EDGE,{"derivedFrom":sQuery(id+"F2.wireOp",EDGE,"E6.5.1.0")}),-1.0]])]});
            var Q12;
            Q12=makeQuery(id+"F2.imprint","IMPRINT",FACE,{"disambiguationData":[TD([[makeQuery(id+"F2.imprint","IMPRINT",EDGE,{"derivedFrom":sQuery(id+"F2.wireOp",EDGE,"E6.6.1.0")}),-1.0]])]});
            var Q13;
            Q13=makeQuery(id+"F2.imprint","IMPRINT",FACE,{"disambiguationData":[TD([[makeQuery(id+"F2.imprint","IMPRINT",EDGE,{"derivedFrom":sQuery(id+"F2.wireOp",EDGE,"E6.6.0.0")}),-1.0]])]});
            var Q14;
            Q14=makeQuery(id+"F2.imprint","IMPRINT",FACE,{"disambiguationData":[TD([[makeQuery(id+"F2.imprint","IMPRINT",EDGE,{"derivedFrom":sQuery(id+"F2.wireOp",EDGE,"E6.7.0.0")}),-1.0]])]});
            var Q15;
            Q15=makeQuery(id+"F2.imprint","IMPRINT",FACE,{"disambiguationData":[TD([[makeQuery(id+"F2.imprint","IMPRINT",EDGE,{"derivedFrom":sQuery(id+"F2.wireOp",EDGE,"E6.7.1.0")}),-1.0]])]});
            var Q16;
            Q16=makeQuery(id+"F2.imprint","IMPRINT",FACE,{"disambiguationData":[TD([[makeQuery(id+"F2.imprint","IMPRINT",EDGE,{"derivedFrom":sQuery(id+"F2.wireOp",EDGE,"E6.8.0.0")}),-1.0]])]});
            var Q17;
            Q17=makeQuery(id+"F2.imprint","IMPRINT",FACE,{"disambiguationData":[TD([[makeQuery(id+"F2.imprint","IMPRINT",EDGE,{"derivedFrom":sQuery(id+"F2.wireOp",EDGE,"E6.8.1.0")}),-1.0]])]});
            var Q18;
            Q18=makeQuery(id+"F2.imprint","IMPRINT",FACE,{"disambiguationData":[TD([[makeQuery(id+"F2.imprint","IMPRINT",EDGE,{"derivedFrom":sQuery(id+"F2.wireOp",EDGE,"E6.9.0.0")}),-1.0]])]});
            var Q19;
            Q19=makeQuery(id+"F2.imprint","IMPRINT",FACE,{"disambiguationData":[TD([[makeQuery(id+"F2.imprint","IMPRINT",EDGE,{"derivedFrom":sQuery(id+"F2.wireOp",EDGE,"E6.10.1.0")}),-1.0]])]});
            var Q20;
            Q20=makeQuery(id+"F2.imprint","IMPRINT",FACE,{"disambiguationData":[TD([[makeQuery(id+"F2.imprint","IMPRINT",EDGE,{"derivedFrom":sQuery(id+"F2.wireOp",EDGE,"E6.10.0.0")}),-1.0]])]});
            var Q21;
            Q21=makeQuery(id+"F2.imprint","IMPRINT",FACE,{"disambiguationData":[TD([[makeQuery(id+"F2.imprint","IMPRINT",EDGE,{"derivedFrom":sQuery(id+"F2.wireOp",EDGE,"E6.9.1.0")}),-1.0]])]});
            var Q22;
            Q22=makeQuery(id+"F2.imprint","IMPRINT",FACE,{"disambiguationData":[TD([[makeQuery(id+"F2.imprint","IMPRINT",EDGE,{"derivedFrom":sQuery(id+"F2.wireOp",EDGE,"E6.11.0.0")}),-1.0]])]});
            var Q23;
            Q23=makeQuery(id+"F2.imprint","IMPRINT",FACE,{"disambiguationData":[TD([[makeQuery(id+"F2.imprint","IMPRINT",EDGE,{"derivedFrom":sQuery(id+"F2.wireOp",EDGE,"E6.11.1.0")}),-1.0]])]});
            var Q24;
            Q24=makeQuery(id+"F2.imprint","IMPRINT",FACE,{"disambiguationData":[TD([[makeQuery(id+"F2.imprint","IMPRINT",EDGE,{"derivedFrom":sQuery(id+"F2.wireOp",EDGE,"E6.12.1.0")}),-1.0]])]});
            var Q25;
            Q25=makeQuery(id+"F2.imprint","IMPRINT",FACE,{"disambiguationData":[TD([[makeQuery(id+"F2.imprint","IMPRINT",EDGE,{"derivedFrom":sQuery(id+"F2.wireOp",EDGE,"E6.12.0.0")}),-1.0]])]});
            var Q26;
            Q26=makeQuery(id+"F2.imprint","IMPRINT",FACE,{"disambiguationData":[TD([[makeQuery(id+"F2.imprint","IMPRINT",EDGE,{"derivedFrom":sQuery(id+"F2.wireOp",EDGE,"E6.13.0.0")}),-1.0]])]});
            var Q27;
            Q27=makeQuery(id+"F2.imprint","IMPRINT",FACE,{"disambiguationData":[TD([[makeQuery(id+"F2.imprint","IMPRINT",EDGE,{"derivedFrom":sQuery(id+"F2.wireOp",EDGE,"E6.13.1.0")}),-1.0]])]});
            var Q28;
            Q28=makeQuery(id+"F2.imprint","IMPRINT",FACE,{"disambiguationData":[TD([[makeQuery(id+"F2.imprint","IMPRINT",EDGE,{"derivedFrom":sQuery(id+"F2.wireOp",EDGE,"E6.14.1.0")}),-1.0]])]});
            var Q29;
            Q29=makeQuery(id+"F2.imprint","IMPRINT",FACE,{"disambiguationData":[TD([[makeQuery(id+"F2.imprint","IMPRINT",EDGE,{"derivedFrom":sQuery(id+"F2.wireOp",EDGE,"E6.14.0.0")}),-1.0]])]});
            var Q30;
            Q30=makeQuery(id+"F2.imprint","IMPRINT",FACE,{"disambiguationData":[TD([[makeQuery(id+"F2.imprint","IMPRINT",EDGE,{"derivedFrom":sQuery(id+"F2.wireOp",EDGE,"E6.15.0.0")}),-1.0]])]});
            var Q31;
            Q31=makeQuery(id+"F2.imprint","IMPRINT",FACE,{"disambiguationData":[TD([[makeQuery(id+"F2.imprint","IMPRINT",EDGE,{"derivedFrom":sQuery(id+"F2.wireOp",EDGE,"E6.15.1.0")}),-1.0]])]});
            var Q32;
            Q32=makeQuery(id+"F2.imprint","IMPRINT",FACE,{"disambiguationData":[TD([[makeQuery(id+"F2.imprint","IMPRINT",EDGE,{"derivedFrom":sQuery(id+"F2.wireOp",EDGE,"E6.16.1.0")}),-1.0]])]});
            var Q33;
            Q33=makeQuery(id+"F2.imprint","IMPRINT",FACE,{"disambiguationData":[TD([[makeQuery(id+"F2.imprint","IMPRINT",EDGE,{"derivedFrom":sQuery(id+"F2.wireOp",EDGE,"E6.16.0.0")}),-1.0]])]});
            var Q34;
            Q34=makeQuery(id+"F2.imprint","IMPRINT",FACE,{"disambiguationData":[TD([[makeQuery(id+"F2.imprint","IMPRINT",EDGE,{"derivedFrom":sQuery(id+"F2.wireOp",EDGE,"E6.17.0.0")}),-1.0]])]});
            var Q35;
            Q35=makeQuery(id+"F2.imprint","IMPRINT",FACE,{"disambiguationData":[TD([[makeQuery(id+"F2.imprint","IMPRINT",EDGE,{"derivedFrom":sQuery(id+"F2.wireOp",EDGE,"E6.17.1.0")}),-1.0]])]});
            var Q36;
            Q36=makeQuery(id+"F2.imprint","IMPRINT",FACE,{"disambiguationData":[TD([[makeQuery(id+"F2.imprint","IMPRINT",EDGE,{"derivedFrom":sQuery(id+"F2.wireOp",EDGE,"E6.18.1.0")}),-1.0]])]});
            var Q37;
            Q37=makeQuery(id+"F2.imprint","IMPRINT",FACE,{"disambiguationData":[TD([[makeQuery(id+"F2.imprint","IMPRINT",EDGE,{"derivedFrom":sQuery(id+"F2.wireOp",EDGE,"E6.18.0.0")}),-1.0]])]});
            var Q38;
            Q38=makeQuery(id+"F2.imprint","IMPRINT",FACE,{"disambiguationData":[TD([[makeQuery(id+"F2.imprint","IMPRINT",EDGE,{"derivedFrom":sQuery(id+"F2.wireOp",EDGE,"E6.19.0.0")}),-1.0]])]});
            var Q39;
            Q39=makeQuery(id+"F2.imprint","IMPRINT",FACE,{"disambiguationData":[TD([[makeQuery(id+"F2.imprint","IMPRINT",EDGE,{"derivedFrom":sQuery(id+"F2.wireOp",EDGE,"E6.19.1.0")}),-1.0]])]});
            var Q40;
            Q40=makeQuery(id+"F2.imprint","IMPRINT",FACE,{"disambiguationData":[TD([[makeQuery(id+"F2.imprint","IMPRINT",EDGE,{"derivedFrom":sQuery(id+"F2.wireOp",EDGE,"E6.20.1.0")}),-1.0]])]});
            var Q41;
            Q41=makeQuery(id+"F2.imprint","IMPRINT",FACE,{"disambiguationData":[TD([[makeQuery(id+"F2.imprint","IMPRINT",EDGE,{"derivedFrom":sQuery(id+"F2.wireOp",EDGE,"E6.20.0.0")}),-1.0]])]});
            var Q42;
            Q42=makeQuery(id+"F2.imprint","IMPRINT",FACE,{"disambiguationData":[TD([[makeQuery(id+"F2.imprint","IMPRINT",EDGE,{"derivedFrom":sQuery(id+"F2.wireOp",EDGE,"E6.21.0.0")}),-1.0]])]});
            var Q43;
            Q43=makeQuery(id+"F2.imprint","IMPRINT",FACE,{"disambiguationData":[TD([[makeQuery(id+"F2.imprint","IMPRINT",EDGE,{"derivedFrom":sQuery(id+"F2.wireOp",EDGE,"E6.21.1.0")}),-1.0]])]});
            var Q44;
            Q44=makeQuery(id+"F2.imprint","IMPRINT",FACE,{"disambiguationData":[TD([[makeQuery(id+"F2.imprint","IMPRINT",EDGE,{"derivedFrom":sQuery(id+"F2.wireOp",EDGE,"E6.22.1.0")}),-1.0]])]});
            var Q45;
            Q45=makeQuery(id+"F2.imprint","IMPRINT",FACE,{"disambiguationData":[TD([[makeQuery(id+"F2.imprint","IMPRINT",EDGE,{"derivedFrom":sQuery(id+"F2.wireOp",EDGE,"E6.22.0.0")}),-1.0]])]});
            var Q46;
            Q46=makeQuery(id+"F2.imprint","IMPRINT",FACE,{"disambiguationData":[TD([[makeQuery(id+"F2.imprint","IMPRINT",EDGE,{"derivedFrom":sQuery(id+"F2.wireOp",EDGE,"E6.23.0.0")}),-1.0]])]});
            var Q47;
            Q47=makeQuery(id+"F2.imprint","IMPRINT",FACE,{"disambiguationData":[TD([[makeQuery(id+"F2.imprint","IMPRINT",EDGE,{"derivedFrom":sQuery(id+"F2.wireOp",EDGE,"E6.23.1.0")}),-1.0]])]});
            extrude(context, id + "F3", {"entities" : qUnion([Q0, Q1, Q2, Q3, Q4, Q5, Q6, Q7, Q8, Q9, Q10, Q11, Q12, Q13, Q14, Q15, Q16, Q17, Q18, Q19, Q20, Q21, Q22, Q23, Q24, Q25, Q26, Q27, Q28, Q29, Q30, Q31, Q32, Q33, Q34, Q35, Q36, Q37, Q38, Q39, Q40, Q41, Q42, Q43, Q44, Q45, Q46, Q47]), "operationType" : NewBodyOperationType.REMOVE, "endBound" : BoundingType.UP_TO_NEXT, "oppositeDirection" : true, "depth" : 25.4 * mm});
        }
    });
